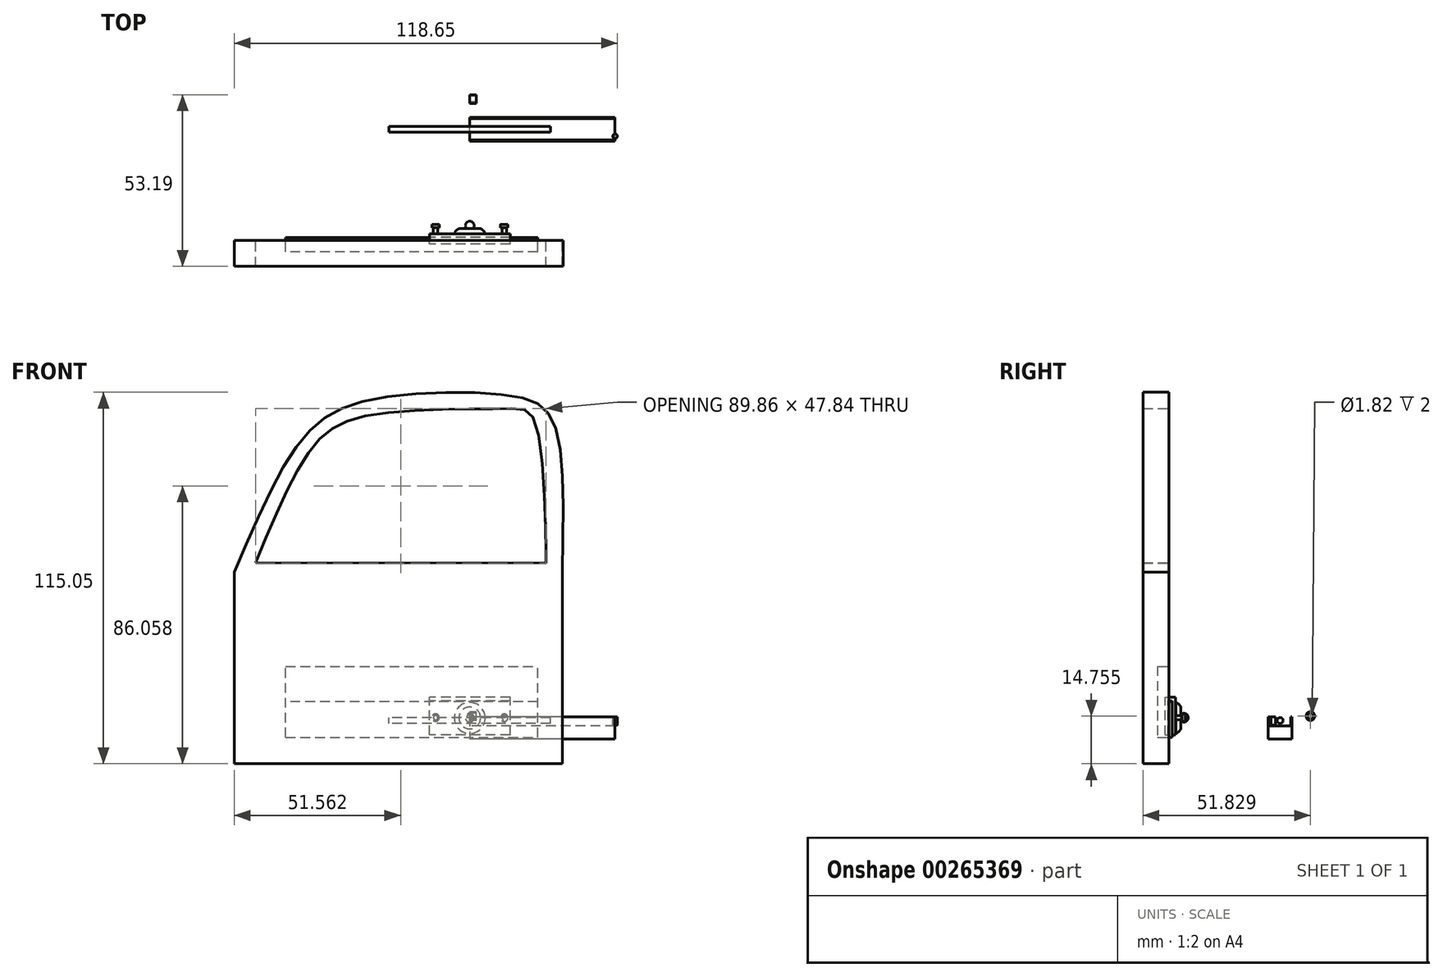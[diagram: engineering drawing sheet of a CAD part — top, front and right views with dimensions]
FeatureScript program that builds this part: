
annotation { "Feature Type Name" : "Feature", "Feature Type Description" : "" }
export const myFeature = defineFeature(function(context is Context, id is Id, definition is map)
    precondition{}
    {
        {
            var Q0;
            Q0=qCreatedBy(makeId("Front.planeOp"),FACE);
            var sketch = newSketch(context, id + "F0", { "sketchPlane" : qUnion([Q0])});
            skLineSegment(sketch, "E0.bottom", {"start": v(28.62, -81.37) * mm, "end": v(-72.94, -81.37) * mm});
            skLineSegment(sketch, "E0.left", {"start": v(28.62, -81.37) * mm, "end": v(28.62, -22.05) * mm});
            skLineSegment(sketch, "E0.right", {"start": v(-72.94, -81.37) * mm, "end": v(-72.94, -22.05) * mm});
            skFitSpline(sketch, "E1", {"points": [v(-72.94, -22.05) * mm, v(-52.29, 18.69) * mm, v(-31.26, 31.27) * mm, v(13.98, 32.4) * mm, v(25.8, 24.7) * mm, v(28.62, -22.05) * mm], "startDerivative": vector(85.44, 201.79) * mm, "endDerivative": vector(-6.45, -241.46) * mm});
            skFitSpline(sketch, "E2", {"points": [v(-66.3, -19.04) * mm, v(-48.72, 16.62) * mm, v(-31.26, 26.57) * mm, v(11.54, 28.64) * mm, v(20.36, 24.32) * mm, v(23.55, -19.23) * mm, v(23.55, -19.42) * mm], "startDerivative": vector(74.67, 181.05) * mm, "endDerivative": vector(0.05, -3.93) * mm});
            skLineSegment(sketch, "E3", {"start": v(-66.3, -19.04) * mm, "end": v(23.55, -19.23) * mm});
            skLineSegment(sketch, "E4.bottom", {"start": v(21.07, -51.16) * mm, "end": v(-57.04, -51.16) * mm});
            skLineSegment(sketch, "E4.top", {"start": v(21.07, -73.16) * mm, "end": v(-57.04, -73.16) * mm});
            skLineSegment(sketch, "E4.left", {"start": v(21.07, -51.16) * mm, "end": v(21.07, -73.16) * mm});
            skLineSegment(sketch, "E4.right", {"start": v(-57.04, -51.16) * mm, "end": v(-57.04, -73.16) * mm});
            skSolve(sketch);
        }
        {
            var Q0;
            Q0=makeQuery(id+"F0.imprint","IMPRINT",FACE,{"disambiguationData":[TD([[makeQuery(id+"F0.imprint","IMPRINT",EDGE,{"derivedFrom":sQuery(id+"F0.wireOp",EDGE,"E0.bottom")}),-1.0]])]});
            var Q1;
            Q1=makeQuery(id+"F0.imprint","IMPRINT",FACE,{"disambiguationData":[TD([[makeQuery(id+"F0.imprint","IMPRINT",EDGE,{"derivedFrom":sQuery(id+"F0.wireOp",EDGE,"E4.bottom")}),1.0]])]});
            var Q2;
            Q2 = qConstructionFilter(qBodyType(qCreatedBy(id + "F0" ,EDGE), BodyType.WIRE), ConstructionObject.NO);
            extrude(context, id + "F1", {"entities" : qUnion([Q0, Q1]), "surfaceEntities" : qUnion([Q2]), "depth" : 8 * mm});
        }
        {
            var Q0;
            Q0=makeQuery(id+"F0.imprint","IMPRINT",FACE,{"disambiguationData":[TD([[makeQuery(id+"F0.imprint","IMPRINT",EDGE,{"derivedFrom":sQuery(id+"F0.wireOp",EDGE,"E4.bottom")}),1.0]])]});
            extrude(context, id + "F2", {"entities" : qUnion([Q0]), "operationType" : NewBodyOperationType.REMOVE, "endBound" : BoundingType.SYMMETRIC, "depth" : 7 * mm});
        }
        {
            var Q0;
            Q0=makeQuery(id+"F1.opExtrude","CAP_FACE",FACE,{"disambiguationData":[OSD([sQuery(id+"F0.wireOp",EDGE,"E0.bottom"),sQuery(id+"F0.wireOp",EDGE,"E0.left"),sQuery(id+"F0.wireOp",EDGE,"E0.right"),sQuery(id+"F0.wireOp",EDGE,"E1"),sQuery(id+"F0.wireOp",EDGE,"E2"),sQuery(id+"F0.wireOp",EDGE,"E3")])],"isStart":true});
            var sketch = newSketch(context, id + "F3", { "sketchPlane" : qUnion([Q0])});
            skLineSegment(sketch, "E5.bottom", {"start": v(-21.07, -73.16) * mm, "end": v(57.04, -73.16) * mm});
            skLineSegment(sketch, "E5.top", {"start": v(-21.07, -62.16) * mm, "end": v(57.04, -62.16) * mm});
            skLineSegment(sketch, "E5.left", {"start": v(-21.07, -73.16) * mm, "end": v(-21.07, -62.16) * mm});
            skLineSegment(sketch, "E5.right", {"start": v(57.04, -73.16) * mm, "end": v(57.04, -62.16) * mm});
            skSolve(sketch);
        }
        {
            var Q0;
            Q0 = qSketchRegion(id + "F3", true);
            extrude(context, id + "F4", {"entities" : qUnion([Q0]), "depth" : 1 * mm});
        }
        {
            var Q0;
            Q0=qCreatedBy(makeId("Right.planeOp"),FACE);
            var sketch = newSketch(context, id + "F5", { "sketchPlane" : qUnion([Q0])});
            skLineSegment(sketch, "E6.bottom", {"start": v(-1.09, -72.45) * mm, "end": v(-0.22, -72.45) * mm});
            skLineSegment(sketch, "E6.top", {"start": v(-1.09, -60.77) * mm, "end": v(2.05, -60.77) * mm});
            skLineSegment(sketch, "E6.left", {"start": v(-1.09, -72.45) * mm, "end": v(-1.09, -60.77) * mm});
            skLineSegment(sketch, "E6.right", {"start": v(2.05, -72.45) * mm, "end": v(2.05, -60.77) * mm});
            skLineSegment(sketch, "E7", {"start": v(-0.22, -72.45) * mm, "end": v(-0.22, -61.9) * mm});
            skLineSegment(sketch, "E8", {"start": v(-0.22, -61.9) * mm, "end": v(1.02, -61.9) * mm});
            skLineSegment(sketch, "E9", {"start": v(1.02, -61.9) * mm, "end": v(1.02, -72.45) * mm});
            skLineSegment(sketch, "E10.trimOffspring", {"start": v(1.02, -72.45) * mm, "end": v(2.05, -72.45) * mm});
            skSolve(sketch);
        }
        {
            var Q0;
            Q0 = qSketchRegion(id + "F5", true);
            extrude(context, id + "F6", {"entities" : qUnion([Q0]), "endBound" : BoundingType.SYMMETRIC, "depth" : 25 * mm});
        }
        {
            var Q0;
            Q0=makeQuery(id+"F6.opExtrude","SWEPT_FACE",FACE,{"disambiguationData":[OSD([sQuery(id+"F5.wireOp",EDGE,"E6.right")])]});
            var sketch = newSketch(context, id + "F7", { "sketchPlane" : qUnion([Q0])});
            skCircle(sketch, "E11", {"center": v(-10.7, -67.1) * mm, "radius": 0.67 * mm});
            skCircle(sketch, "E12", {"center": v(10.58, -67.1) * mm, "radius": 0.68 * mm});
            skSolve(sketch);
        }
        {
            var Q0;
            Q0 = qSketchRegion(id + "F7", true);
            extrude(context, id + "F8", {"entities" : qUnion([Q0]), "operationType" : NewBodyOperationType.ADD, "depth" : 2 * mm});
        }
        {
            var Q0;
            Q0=makeQuery(id+"F8.opExtrude","CAP_FACE",FACE,{"disambiguationData":[OSD([sQuery(id+"F7.wireOp",EDGE,"E11")])],"isStart":false});
            var sketch = newSketch(context, id + "F9", { "sketchPlane" : qUnion([Q0])});
            skCircle(sketch, "E13", {"center": v(-10.7, -67.1) * mm, "radius": 1.15 * mm});
            skCircle(sketch, "E14", {"center": v(10.6, -67.07) * mm, "radius": 1.15 * mm});
            skSolve(sketch);
        }
        {
            var Q0;
            Q0 = qSketchRegion(id + "F9", true);
            extrude(context, id + "F10", {"entities" : qUnion([Q0]), "operationType" : NewBodyOperationType.ADD, "depth" : 1 * mm});
        }
        {
            var Q0;
            Q0=qCreatedBy(makeId("Right.planeOp"),FACE);
            var sketch = newSketch(context, id + "F11", { "sketchPlane" : qUnion([Q0])});
            skLineSegment(sketch, "E15.bottom", {"start": v(2.07, -62.39) * mm, "end": v(2.13, -62.39) * mm});
            skLineSegment(sketch, "E15.top", {"start": v(2.07, -67.18) * mm, "end": v(3.69, -67.18) * mm});
            skLineSegment(sketch, "E15.left", {"start": v(2.07, -62.39) * mm, "end": v(2.07, -67.18) * mm});
            skLineSegment(sketch, "E15.right", {"start": v(3.69, -63.81) * mm, "end": v(3.69, -67.18) * mm});
            skLineSegment(sketch, "E16", {"start": v(2.07, -67.18) * mm, "end": v(6.73, -67.18) * mm, "construction": true});
            skArc(sketch, "E17", {"start": v(3.69, -63.81) * mm, "mid": v(3.07, -62.93) * mm, "end": v(2.13, -62.39) * mm});
            skPoint(sketch, "E18", {"position": v(2.07, -64.78) * mm});
            skSolve(sketch);
        }
        {
            var Q0;
            Q0=makeQuery(id+"F11.imprint","IMPRINT",FACE,{"disambiguationData":[TD([[makeQuery(id+"F11.imprint","IMPRINT",EDGE,{"derivedFrom":sQuery(id+"F11.wireOp",EDGE,"E15.bottom")}),-1.0]])]});
            var Q1;
            Q1=sQuery(id+"F11.wireOp",EDGE,"E16");
            revolve(context, id + "F12", {"entities" : qUnion([Q0]), "axis" : qUnion([Q1]), "revolveType" : RevolveType.FULL});
        }
        {
            var Q0;
            Q0=qCreatedBy(makeId("Right.planeOp"),FACE);
            var sketch = newSketch(context, id + "F13", { "sketchPlane" : qUnion([Q0])});
            skArc(sketch, "E19", {"start": v(6, -67.1) * mm, "mid": v(4.64, -65.75) * mm, "end": v(3.3, -67.1) * mm});
            skLineSegment(sketch, "E20", {"start": v(2.6, -67.1) * mm, "end": v(7.1, -67.1) * mm, "construction": true});
            skLineSegment(sketch, "E21", {"start": v(3.3, -67.1) * mm, "end": v(6, -67.1) * mm});
            skSolve(sketch);
        }
        {
            var Q0;
            Q0=makeQuery(id+"F13.imprint","IMPRINT",FACE,{"disambiguationData":[TD([[makeQuery(id+"F13.imprint","IMPRINT",EDGE,{"derivedFrom":sQuery(id+"F13.wireOp",EDGE,"E19")}),1.0]])]});
            var Q1;
            Q1=sQuery(id+"F13.wireOp",EDGE,"E20");
            revolve(context, id + "F14", {"operationType" : NewBodyOperationType.ADD, "entities" : qUnion([Q0]), "axis" : qUnion([Q1]), "revolveType" : RevolveType.FULL});
        }
        {
            var Q0;
            Q0=qCreatedBy(makeId("Right.planeOp"),FACE);
            var sketch = newSketch(context, id + "F15", { "sketchPlane" : qUnion([Q0])});
            skCircle(sketch, "E22", {"center": v(34.46, -67.96) * mm, "radius": 0.91 * mm});
            skCircle(sketch, "E23", {"center": v(43.83, -66.62) * mm, "radius": 0.91 * mm});
            skCircle(sketch, "E24", {"center": v(43.83, -66.62) * mm, "radius": 1.36 * mm});
            skSolve(sketch);
        }
        {
            var Q0;
            Q0=makeQuery(id+"F15.imprint","IMPRINT",FACE,{"disambiguationData":[TD([[makeQuery(id+"F15.imprint","IMPRINT",EDGE,{"derivedFrom":sQuery(id+"F15.wireOp",EDGE,"E22")}),1.0]])]});
            extrude(context, id + "F16", {"entities" : qUnion([Q0]), "endBound" : BoundingType.SYMMETRIC, "depth" : 50 * mm});
        }
        {
            var Q0;
            Q0=qCreatedBy(makeId("Right.planeOp"),FACE);
            var sketch = newSketch(context, id + "F17", { "sketchPlane" : qUnion([Q0])});
            skLineSegment(sketch, "E25.bottom", {"start": v(30.78, -66.8) * mm, "end": v(31.2, -66.8) * mm});
            skLineSegment(sketch, "E25.top", {"start": v(30.78, -73.66) * mm, "end": v(38.17, -73.66) * mm});
            skLineSegment(sketch, "E25.left", {"start": v(30.78, -66.8) * mm, "end": v(30.78, -73.66) * mm});
            skLineSegment(sketch, "E25.right", {"start": v(38.17, -66.8) * mm, "end": v(38.17, -73.66) * mm});
            skLineSegment(sketch, "E26.top", {"start": v(31.2, -69.63) * mm, "end": v(37.78, -69.63) * mm});
            skLineSegment(sketch, "E26.left", {"start": v(31.2, -66.8) * mm, "end": v(31.2, -69.63) * mm});
            skLineSegment(sketch, "E26.right", {"start": v(37.78, -66.8) * mm, "end": v(37.78, -69.63) * mm});
            skLineSegment(sketch, "E27.trimOffspring", {"start": v(37.78, -66.8) * mm, "end": v(38.17, -66.8) * mm});
            skSolve(sketch);
        }
        {
            var Q0;
            Q0 = qSketchRegion(id + "F17", true);
            extrude(context, id + "F18", {"entities" : qUnion([Q0]), "depth" : 45 * mm});
        }
        {
            var Q0;
            Q0=makeQuery(id+"F18.opExtrude","CAP_FACE",FACE,{"disambiguationData":[OSD([sQuery(id+"F17.wireOp",EDGE,"E25.bottom"),sQuery(id+"F17.wireOp",EDGE,"E25.top"),sQuery(id+"F17.wireOp",EDGE,"E25.left"),sQuery(id+"F17.wireOp",EDGE,"E25.right"),sQuery(id+"F17.wireOp",EDGE,"E26.top"),sQuery(id+"F17.wireOp",EDGE,"E26.left"),sQuery(id+"F17.wireOp",EDGE,"E26.right"),sQuery(id+"F17.wireOp",EDGE,"E27.trimOffspring")])],"isStart":false});
            var sketch = newSketch(context, id + "F19", { "sketchPlane" : qUnion([Q0])});
            skLineSegment(sketch, "E28.bottom", {"start": v(32.32, -66.8) * mm, "end": v(33.03, -66.8) * mm});
            skLineSegment(sketch, "E28.top", {"start": v(32.32, -69.36) * mm, "end": v(33.03, -69.36) * mm});
            skLineSegment(sketch, "E28.right", {"start": v(33.03, -66.8) * mm, "end": v(33.03, -69.36) * mm});
            skLineSegment(sketch, "E29", {"start": v(32.32, -66.8) * mm, "end": v(32.32, -69.84) * mm, "construction": true});
            skPoint(sketch, "E29.endSnap0", {"position": v(32.32, -69.36) * mm});
            skPoint(sketch, "E28.left.start.orphan", {"position": v(31.61, -66.8) * mm});
            skPoint(sketch, "E30.orphan", {"position": v(31.61, -69.36) * mm});
            skLineSegment(sketch, "E31", {"start": v(32.32, -66.8) * mm, "end": v(32.32, -69.36) * mm});
            skSolve(sketch);
        }
        {
            var Q0;
            Q0=makeQuery(id+"F19.imprint","IMPRINT",FACE,{"disambiguationData":[TD([[makeQuery(id+"F19.imprint","IMPRINT",EDGE,{"derivedFrom":sQuery(id+"F19.wireOp",EDGE,"E28.bottom")}),-1.0]])]});
            var Q1;
            Q1=sQuery(id+"F19.wireOp",EDGE,"E29");
            revolve(context, id + "F20", {"entities" : qUnion([Q0]), "axis" : qUnion([Q1]), "revolveType" : RevolveType.FULL});
        }
        {
            var Q0;
            Q0=makeQuery(id+"F15.imprint","IMPRINT",FACE,{"disambiguationData":[TD([[makeQuery(id+"F15.imprint","IMPRINT",EDGE,{"derivedFrom":sQuery(id+"F15.wireOp",EDGE,"E23")}),-1.0]])]});
            extrude(context, id + "F21", {"entities" : qUnion([Q0]), "operationType" : NewBodyOperationType.ADD, "depth" : 2 * mm});
        }
    });
